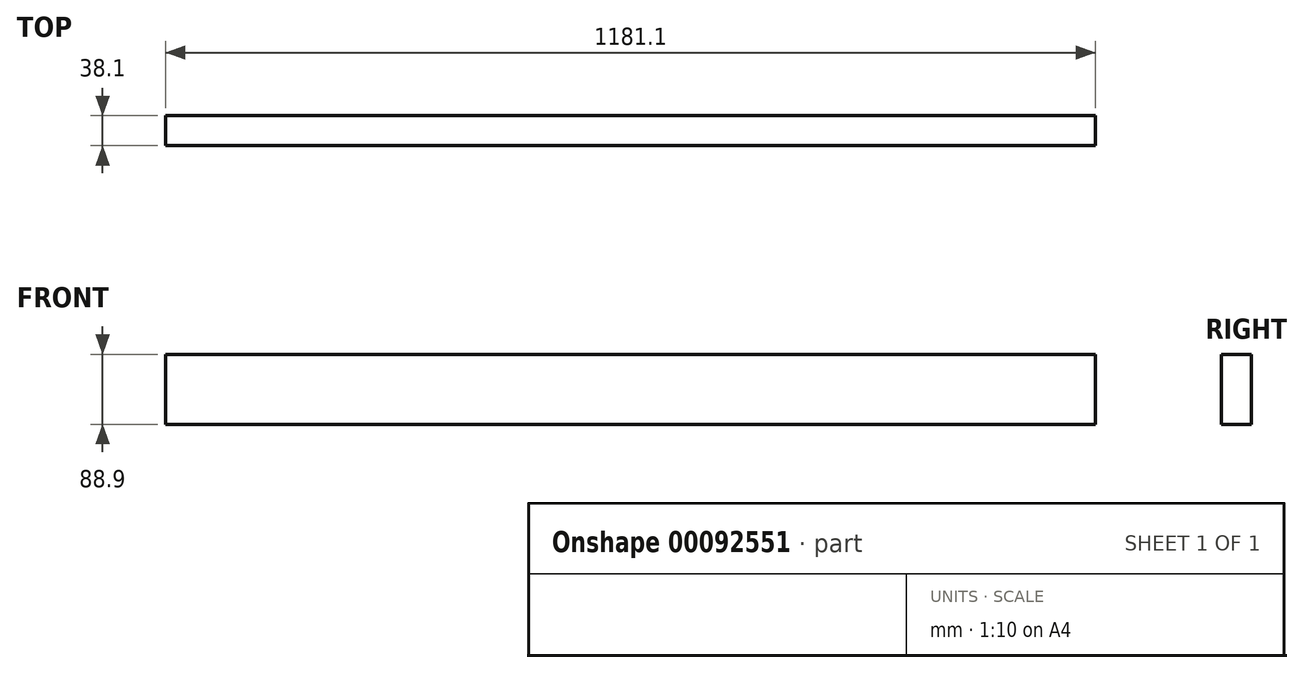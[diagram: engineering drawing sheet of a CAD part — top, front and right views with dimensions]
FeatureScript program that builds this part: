
annotation { "Feature Type Name" : "Feature", "Feature Type Description" : "" }
export const myFeature = defineFeature(function(context is Context, id is Id, definition is map)
    precondition{}
    {
        {
            var Q0;
            Q0=qCreatedBy(makeId("Front.planeOp"),FACE);
            var sketch = newSketch(context, id + "F0", { "sketchPlane" : qUnion([Q0])});
            skLineSegment(sketch, "E0.bottom", {"start": v(-589.23, -40.39) * mm, "end": v(591.87, -40.39) * mm});
            skLineSegment(sketch, "E0.top", {"start": v(-589.23, -129.29) * mm, "end": v(591.87, -129.29) * mm});
            skLineSegment(sketch, "E0.left", {"start": v(-589.23, -40.39) * mm, "end": v(-589.23, -129.29) * mm});
            skLineSegment(sketch, "E0.right", {"start": v(591.87, -40.39) * mm, "end": v(591.87, -129.29) * mm});
            skSolve(sketch);
        }
        {
            var Q0;
            Q0=makeQuery(id+"F0.imprint","IMPRINT",FACE,{"disambiguationData":[TD([[makeQuery(id+"F0.imprint","IMPRINT",EDGE,{"derivedFrom":sQuery(id+"F0.wireOp",EDGE,"E0.bottom")}),-1.0]])]});
            extrude(context, id + "F1", {"entities" : qUnion([Q0]), "depth" : 38.1 * mm});
        }
    });
